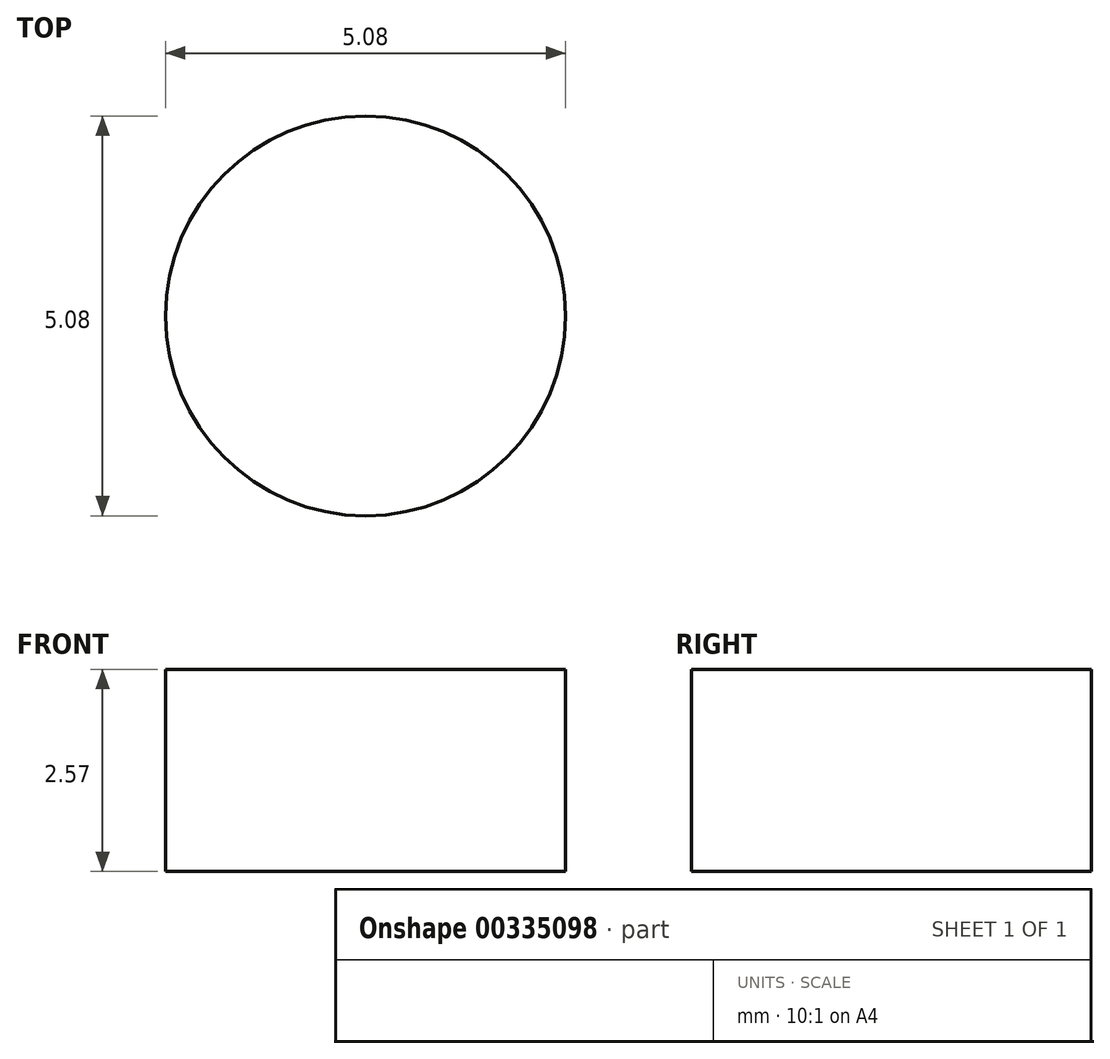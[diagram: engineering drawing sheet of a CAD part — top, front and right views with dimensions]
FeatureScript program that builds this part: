
annotation { "Feature Type Name" : "Feature", "Feature Type Description" : "" }
export const myFeature = defineFeature(function(context is Context, id is Id, definition is map)
    precondition{}
    {
        {
            var Q0;
            Q0=qCreatedBy(makeId("Top.planeOp"),FACE);
            var sketch = newSketch(context, id + "F0", { "sketchPlane" : qUnion([Q0])});
            skCircle(sketch, "E0", {"center": v(0, 0) * mm, "radius": 2.54 * mm});
            skSolve(sketch);
        }
        {
            var Q0;
            Q0 = qSketchRegion(id + "F0", true);
            extrude(context, id + "F1", {"entities" : qUnion([Q0]), "depth" : 10.16 * mm});
        }
        {
            var Q0;
            Q0=qCreatedBy(makeId("Top.planeOp"),FACE);
            cPlane(context, id + "F2", {"entities" : qUnion([Q0]), "cplaneType" : CPlaneType.OFFSET, "offset" : 10.2 * mm, "width" : 152.4 * mm, "height" : 152.4 * mm});
        }
        {
            var Q0;
            Q0=qCreatedBy(id+"F2.planeOp",FACE);
            var sketch = newSketch(context, id + "F3", { "sketchPlane" : qUnion([Q0])});
            skCircle(sketch, "E1", {"center": v(0, 0) * mm, "radius": 2.54 * mm});
            skSolve(sketch);
        }
        {
            var Q0;
            Q0 = qSketchRegion(id + "F3", true);
            extrude(context, id + "F4", {"entities" : qUnion([Q0]), "operationType" : NewBodyOperationType.REMOVE, "oppositeDirection" : true, "depth" : 7.62 * mm});
        }
    });
